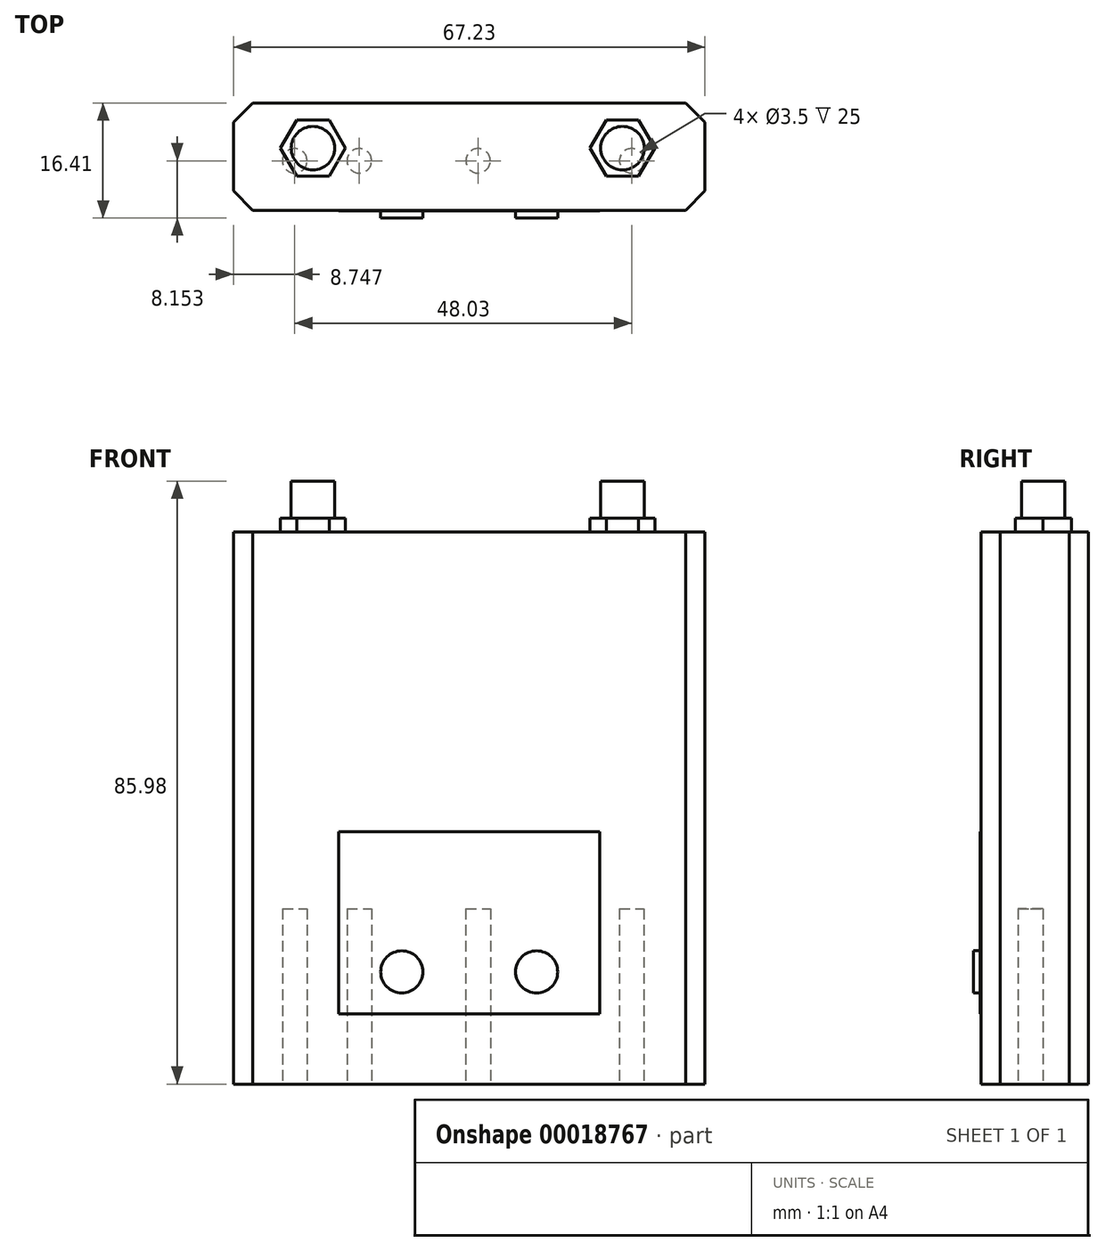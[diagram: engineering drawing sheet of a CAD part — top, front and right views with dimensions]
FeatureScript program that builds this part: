
annotation { "Feature Type Name" : "Feature", "Feature Type Description" : "" }
export const myFeature = defineFeature(function(context is Context, id is Id, definition is map)
    precondition{}
    {
        {
            var Q0;
            Q0=qCreatedBy(makeId("Top.planeOp"),FACE);
            var sketch = newSketch(context, id + "F0", { "sketchPlane" : qUnion([Q0])});
            skLineSegment(sketch, "E0.bottom", {"start": v(-31.85, 6.63) * mm, "end": v(35.38, 6.63) * mm});
            skLineSegment(sketch, "E0.top", {"start": v(-31.85, -8.68) * mm, "end": v(35.38, -8.68) * mm});
            skLineSegment(sketch, "E0.left", {"start": v(-31.85, 6.63) * mm, "end": v(-31.85, -8.68) * mm});
            skLineSegment(sketch, "E0.right", {"start": v(35.38, 6.63) * mm, "end": v(35.38, -8.68) * mm});
            skSolve(sketch);
        }
        {
            var Q0;
            Q0 = qSketchRegion(id + "F0", true);
            extrude(context, id + "F1", {"entities" : qUnion([Q0]), "depth" : 78.7 * mm});
        }
        {
            var Q0;
            Q0=makeQuery(id+"F1.opExtrude","CAP_FACE",FACE,{"disambiguationData":[OSD([sQuery(id+"F0.wireOp",EDGE,"E0.bottom"),sQuery(id+"F0.wireOp",EDGE,"E0.top"),sQuery(id+"F0.wireOp",EDGE,"E0.left"),sQuery(id+"F0.wireOp",EDGE,"E0.right")])],"isStart":true});
            var sketch = newSketch(context, id + "F2", { "sketchPlane" : qUnion([Q0])});
            skCircle(sketch, "E1", {"center": v(-23.1, 1.63) * mm, "radius": 1.75 * mm});
            skCircle(sketch, "E2", {"center": v(-13.9, 1.63) * mm, "radius": 1.75 * mm});
            skCircle(sketch, "E3", {"center": v(3.03, 1.63) * mm, "radius": 1.75 * mm});
            skCircle(sketch, "E4", {"center": v(24.93, 1.63) * mm, "radius": 1.75 * mm});
            skSolve(sketch);
        }
        {
            var Q0;
            Q0 = qSketchRegion(id + "F2", true);
            extrude(context, id + "F3", {"entities" : qUnion([Q0]), "operationType" : NewBodyOperationType.REMOVE, "oppositeDirection" : true, "depth" : 25 * mm});
        }
        {
            var Q0;
            Q0=makeQuery(id+"F1.opExtrude","CAP_FACE",FACE,{"disambiguationData":[OSD([sQuery(id+"F0.wireOp",EDGE,"E0.bottom"),sQuery(id+"F0.wireOp",EDGE,"E0.top"),sQuery(id+"F0.wireOp",EDGE,"E0.left"),sQuery(id+"F0.wireOp",EDGE,"E0.right")])],"isStart":false});
            var sketch = newSketch(context, id + "F4", { "sketchPlane" : qUnion([Q0])});
            skCircle(sketch, "E5.cCircle", {"center": v(23.6, 0.18) * mm, "radius": 4 * mm, "construction": true});
            skLineSegment(sketch, "E5.0", {"start": v(21.3, 4.18) * mm, "end": v(25.92, 4.18) * mm});
            skLineSegment(sketch, "E5.1", {"start": v(25.92, 4.18) * mm, "end": v(28.23, 0.18) * mm});
            skLineSegment(sketch, "E5.2", {"start": v(28.23, 0.18) * mm, "end": v(25.92, -3.82) * mm});
            skLineSegment(sketch, "E5.3", {"start": v(25.92, -3.82) * mm, "end": v(21.3, -3.82) * mm});
            skLineSegment(sketch, "E5.4", {"start": v(21.3, -3.82) * mm, "end": v(18.99, 0.18) * mm});
            skLineSegment(sketch, "E5.5", {"start": v(18.99, 0.18) * mm, "end": v(21.3, 4.18) * mm});
            skPoint(sketch, "E5.0.midPoint", {"position": v(23.6, 4.18) * mm});
            skCircle(sketch, "E6.cCircle", {"center": v(-20.51, 0.18) * mm, "radius": 4 * mm, "construction": true});
            skLineSegment(sketch, "E6.0", {"start": v(-22.82, 4.18) * mm, "end": v(-18.2, 4.18) * mm});
            skLineSegment(sketch, "E6.1", {"start": v(-18.2, 4.18) * mm, "end": v(-15.9, 0.18) * mm});
            skLineSegment(sketch, "E6.2", {"start": v(-15.9, 0.18) * mm, "end": v(-18.2, -3.82) * mm});
            skLineSegment(sketch, "E6.3", {"start": v(-18.2, -3.82) * mm, "end": v(-22.82, -3.82) * mm});
            skLineSegment(sketch, "E6.4", {"start": v(-22.82, -3.82) * mm, "end": v(-25.13, 0.18) * mm});
            skLineSegment(sketch, "E6.5", {"start": v(-25.13, 0.18) * mm, "end": v(-22.82, 4.18) * mm});
            skPoint(sketch, "E6.0.midPoint", {"position": v(-20.51, 4.18) * mm});
            skCircle(sketch, "E7", {"center": v(-20.51, 0.18) * mm, "radius": 3.1 * mm});
            skCircle(sketch, "E8", {"center": v(23.6, 0.18) * mm, "radius": 3.1 * mm});
            skSolve(sketch);
        }
        {
            var Q0;
            Q0 = qSketchRegion(id + "F4", true);
            extrude(context, id + "F5", {"entities" : qUnion([Q0]), "operationType" : NewBodyOperationType.ADD, "depth" : 2 * mm});
        }
        {
            var Q0;
            Q0=makeQuery(id+"F5.boolean.opBoolean","SPLIT",FACE,{"disambiguationData":[TD([makeQuery(id+"F5.opExtrude","SWEPT_FACE",FACE,{"disambiguationData":[OSD([sQuery(id+"F4.wireOp",EDGE,"E7")])]})])],"derivedFrom":makeQuery(id+"F1.opExtrude","CAP_FACE",FACE,{"disambiguationData":[OSD([sQuery(id+"F0.wireOp",EDGE,"E0.bottom"),sQuery(id+"F0.wireOp",EDGE,"E0.top"),sQuery(id+"F0.wireOp",EDGE,"E0.left"),sQuery(id+"F0.wireOp",EDGE,"E0.right")])],"isStart":false})});
            var Q1;
            Q1=makeQuery(id+"F5.boolean.opBoolean","SPLIT",FACE,{"disambiguationData":[TD([makeQuery(id+"F5.opExtrude","SWEPT_FACE",FACE,{"disambiguationData":[OSD([sQuery(id+"F4.wireOp",EDGE,"E8")])]})])],"derivedFrom":makeQuery(id+"F1.opExtrude","CAP_FACE",FACE,{"disambiguationData":[OSD([sQuery(id+"F0.wireOp",EDGE,"E0.bottom"),sQuery(id+"F0.wireOp",EDGE,"E0.top"),sQuery(id+"F0.wireOp",EDGE,"E0.left"),sQuery(id+"F0.wireOp",EDGE,"E0.right")])],"isStart":false})});
            extrude(context, id + "F6", {"entities" : qUnion([Q0, Q1]), "operationType" : NewBodyOperationType.ADD, "depth" : 7.28 * mm});
        }
        {
            var Q0;
            Q0=makeQuery(id+"F1.opExtrude","SWEPT_FACE",FACE,{"disambiguationData":[OSD([sQuery(id+"F0.wireOp",EDGE,"E0.top")])]});
            var sketch = newSketch(context, id + "F7", { "sketchPlane" : qUnion([Q0])});
            skLineSegment(sketch, "E9.bottom", {"start": v(-16.85, 36) * mm, "end": v(20.38, 36) * mm});
            skLineSegment(sketch, "E9.top", {"start": v(-16.85, 10) * mm, "end": v(20.38, 10) * mm});
            skLineSegment(sketch, "E9.left", {"start": v(-16.85, 36) * mm, "end": v(-16.85, 10) * mm});
            skLineSegment(sketch, "E9.right", {"start": v(20.38, 36) * mm, "end": v(20.38, 10) * mm});
            skSolve(sketch);
        }
        {
            var Q0;
            Q0 = qSketchRegion(id + "F7", true);
            extrude(context, id + "F8", {"entities" : qUnion([Q0]), "operationType" : NewBodyOperationType.ADD, "depth" : .1 * mm});
        }
        {
            var Q0;
            Q0=makeQuery(id+"F8.opExtrude","CAP_FACE",FACE,{"disambiguationData":[OSD([sQuery(id+"F7.wireOp",EDGE,"E9.bottom"),sQuery(id+"F7.wireOp",EDGE,"E9.top"),sQuery(id+"F7.wireOp",EDGE,"E9.left"),sQuery(id+"F7.wireOp",EDGE,"E9.right")])],"isStart":false});
            var sketch = newSketch(context, id + "F9", { "sketchPlane" : qUnion([Q0])});
            skCircle(sketch, "E10", {"center": v(-7.85, 16) * mm, "radius": 3 * mm});
            skCircle(sketch, "E11", {"center": v(11.38, 16) * mm, "radius": 3 * mm});
            skSolve(sketch);
        }
        {
            var Q0;
            Q0 = qSketchRegion(id + "F9", true);
            extrude(context, id + "F10", {"entities" : qUnion([Q0]), "operationType" : NewBodyOperationType.ADD, "depth" : 1 * mm});
        }
        {
            var Q0;
            Q0=makeQuery(id+"F1.opExtrude","SWEPT_EDGE",EDGE,{"disambiguationData":[OSD([sQuery(id+"F0.wireOp",EDGE,"E0.top"),sQuery(id+"F0.wireOp",EDGE,"E0.right")])]});
            var Q1;
            Q1=makeQuery(id+"F1.opExtrude","SWEPT_EDGE",EDGE,{"disambiguationData":[OSD([sQuery(id+"F0.wireOp",EDGE,"E0.bottom"),sQuery(id+"F0.wireOp",EDGE,"E0.right")])]});
            var Q2;
            Q2=makeQuery(id+"F1.opExtrude","SWEPT_EDGE",EDGE,{"disambiguationData":[OSD([sQuery(id+"F0.wireOp",EDGE,"E0.bottom"),sQuery(id+"F0.wireOp",EDGE,"E0.left")])]});
            var Q3;
            Q3=makeQuery(id+"F1.opExtrude","SWEPT_EDGE",EDGE,{"disambiguationData":[OSD([sQuery(id+"F0.wireOp",EDGE,"E0.top"),sQuery(id+"F0.wireOp",EDGE,"E0.left")])]});
            chamfer(context, id + "F11", {"entities" : qUnion([Q0, Q1, Q2, Q3]), "width" : 2.75 * mm, "tangentPropagation" : true});
        }
    });
